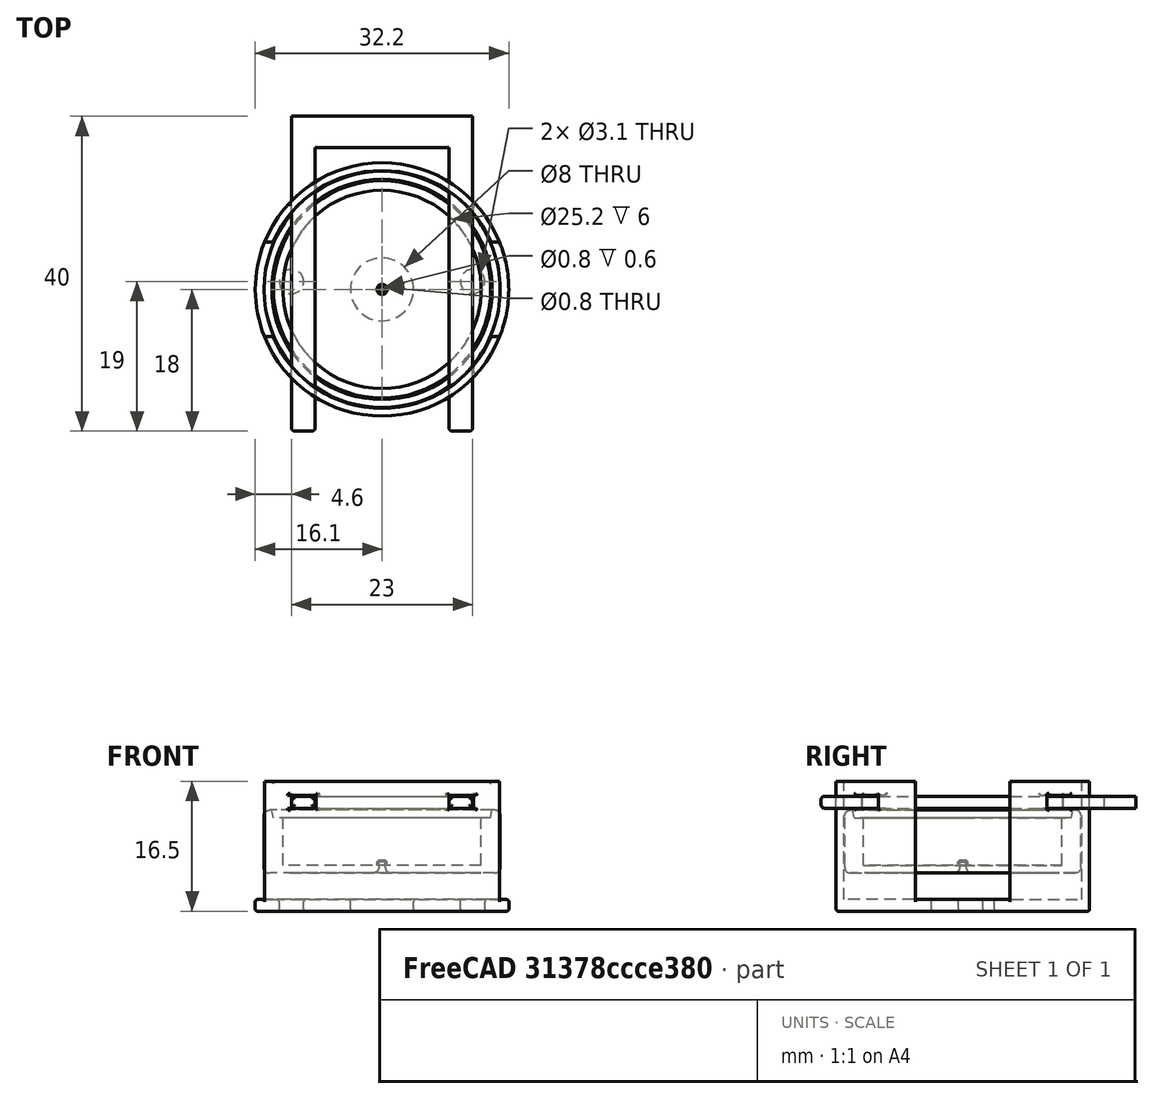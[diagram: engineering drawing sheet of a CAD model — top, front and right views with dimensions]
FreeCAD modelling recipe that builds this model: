
FCSTD DOCUMENT  (FreeCAD 0.18R16131 (Git))
Label: microfluidic_testsetup_v1
License: All rights reserved
LicenseURL: http://en.wikipedia.org/wiki/All_rights_reserved
objects: Part::Cylinder×13, Part::Cut×10, Part::Fillet×7, Part::Box×7, Part::MultiFuse×5, Part::Chamfer×1, Part::Cone×1
note: 44 computed .brp shape members not serialized (recipe doc carries the construction recipe); baked Part::Feature solids carry a one-line shape summary decoded from their .brp

FEATURE [Part::Cylinder] Cylinder
  Angle = 360
  AttacherType = Attacher::AttachEngine3D
  Height = 8
  Radius = 15
FEATURE [Part::Cylinder] Cylinder001
  Angle = 360
  AttacherType = Attacher::AttachEngine3D
  Height = 8
  Radius = 12.6
FEATURE [Part::Cut] Cut
  Base = -> Cylinder
  Tool = -> Cylinder001
FEATURE [Part::Cylinder] Cylinder002
  Angle = 360
  AttacherType = Attacher::AttachEngine3D
  Height = 1
  Radius = 15
FEATURE [Part::MultiFuse] Fusion
  Shapes = -> [Cylinder002,Cut]
FEATURE [Part::Cylinder] Cylinder005
  Angle = 360
  AttacherType = Attacher::AttachEngine3D
  Height = 1
  Radius = 0.4
FEATURE [Part::Cut] Cut001
  Base = -> Fusion
  Tool = -> Cylinder005
FEATURE [Part::Cylinder] Cylinder004
  Angle = 360
  AttacherType = Attacher::AttachEngine3D
  Height = 0.6
  Placement = pos=(0,0,1) rot=(0,0,1;0rad)
  Radius = 0.4
FEATURE [Part::Cylinder] Cylinder003
  Angle = 360
  AttacherType = Attacher::AttachEngine3D
  Height = 0.6
  Placement = pos=(0,0,1) rot=(0,0,1;0rad)
  Radius = 0.65
FEATURE [Part::Cut] Cut002
  Base = -> Cylinder003
  Tool = -> Cylinder004
FEATURE [Part::Chamfer] Chamfer
  Base = -> Cut002
  Edges = 1 edges r=0.2: [Edge1]
FEATURE [Part::Cylinder] Cylinder006
  Angle = 360
  AttacherType = Attacher::AttachEngine3D
  Height = 1
  Placement = pos=(0,0,7) rot=(0,0,1;0rad)
  Radius = 14
FEATURE [Part::Cut] Cut003
  Base = -> Cut001
  Tool = -> Cylinder006
FEATURE [Part::Fillet] Fillet
  Base = -> Cut003
  Edges = 1 edges r=0.7: [Edge5]
FEATURE [Part::Fillet] Fillet001
  Base = -> Fillet
  Edges = 1 edges r=0.7: [Edge7]
FEATURE [Part::Fillet] Fillet002
  Base = -> Fillet001
  Edges = 1 edges r=0.8: [Edge11]
FEATURE [Part::Cone] Cone
  Angle = 360
  AttacherType = Attacher::AttachEngine3D
  Height = 1
  Placement = pos=(0,0,7) rot=(0,0,1;0rad)
  Radius1 = 13.8
  Radius2 = 14
FEATURE [Part::Cylinder] Cylinder007
  Angle = 360
  AttacherType = Attacher::AttachEngine3D
  Height = 1
  Placement = pos=(0,0,7) rot=(0,0,1;0rad)
  Radius = 14
FEATURE [Part::Cut] Cut004
  Base = -> Cylinder007
  Tool = -> Cone
FEATURE [Part::MultiFuse] Fusion001
  Placement = pos=(0,0,3.35) rot=(0,0,1;0rad)
  Shapes = -> [Cut004,Fillet002,Chamfer]
FEATURE [Part::Cylinder] Cylinder008
  Angle = 360
  AttacherType = Attacher::AttachEngine3D
  Height = 16.5
  Placement = pos=(0,0,-1.5) rot=(0,0,1;0rad)
  Radius = 16.1
FEATURE [Part::Cylinder] Cylinder009
  Angle = 360
  AttacherType = Attacher::AttachEngine3D
  Height = 16.5
  Radius = 15.1
FEATURE [Part::Cut] Cut005
  Base = -> Cylinder008
  Tool = -> Cylinder009
FEATURE [Part::Cylinder] Cylinder010
  Angle = 360
  AttacherType = Attacher::AttachEngine3D
  Height = 10
  Placement = pos=(0,0,-2) rot=(0,0,1;0rad)
  Radius = 4
FEATURE [Part::Cut] Cut006
  Base = -> Cut005
  Tool = -> Cylinder010
FEATURE [Part::Box] Box  label="Cube"
  AttacherType = Attacher::AttachEngine3D
  Height = 1.5
  Length = 3
  Placement = pos=(-11.5,-18,11.6) rot=(0,0,1;0rad)
  Width = 36
FEATURE [Part::Box] Box001  label="Cube001"
  AttacherType = Attacher::AttachEngine3D
  Height = 1.5
  Length = 3
  Placement = pos=(8.5,-18,11.6) rot=(0,0,1;0rad)
  Width = 36
FEATURE [Part::Box] Box002  label="Cube002"
  AttacherType = Attacher::AttachEngine3D
  Height = 1.5
  Length = 23
  Placement = pos=(-11.5,18,11.6) rot=(0,0,1;0rad)
  Width = 4
FEATURE [Part::MultiFuse] Fusion002
  Shapes = -> [Box,Box002,Box001]
FEATURE [Part::Box] Box003  label="Cube003"
  AttacherType = Attacher::AttachEngine3D
  Height = 20
  Length = 35
  Placement = pos=(-17.5,-6,0) rot=(0,0,1;0rad)
  Width = 12
FEATURE [Part::Cut] Cut007
  Base = -> Cut006
  Tool = -> Box003
FEATURE [Part::Cylinder] Cylinder011
  Angle = 360
  AttacherType = Attacher::AttachEngine3D
  Height = 10
  Placement = pos=(-11.5,1,-2) rot=(0,0,1;0rad)
  Radius = 1.55
FEATURE [Part::Cylinder] Cylinder012
  Angle = 360
  AttacherType = Attacher::AttachEngine3D
  Height = 10
  Placement = pos=(11.5,1,-2) rot=(0,0,1;0rad)
  Radius = 1.55
FEATURE [Part::MultiFuse] Fusion003
  Shapes = -> [Cylinder012,Cylinder011]
FEATURE [Part::Cut] Cut008
  Base = -> Cut007
  Tool = -> Fusion003
FEATURE [Part::Box] Box004  label="Cube004"
  AttacherType = Attacher::AttachEngine3D
  Height = 1.6
  Length = 3.1
  Placement = pos=(-11.5,-18,11.6) rot=(0,0,1;0rad)
  Width = 36
FEATURE [Part::Box] Box005  label="Cube005"
  AttacherType = Attacher::AttachEngine3D
  Height = 1.5
  Length = 23
  Placement = pos=(-11.5,18,11.6) rot=(0,0,1;0rad)
  Width = 4
FEATURE [Part::Box] Box006  label="Cube006"
  AttacherType = Attacher::AttachEngine3D
  Height = 1.6
  Length = 3.1
  Placement = pos=(8.5,-18,11.6) rot=(0,0,1;0rad)
  Width = 36
FEATURE [Part::MultiFuse] Fusion004
  Shapes = -> [Box004,Box005,Box006]
FEATURE [Part::Cut] Cut009
  Base = -> Cut008
  Tool = -> Fusion004
FEATURE [Part::Fillet] Fillet003
  Base = -> Cut009
  Edges = 12 edges r=0.3: [Edge3,Edge7,Edge10,Edge29,Edge31,Edge35,Edge37,Edge40,Edge47,Edge83,Edge84,Edge85]
FEATURE [Part::Fillet] Fillet004
  Base = -> Fillet003
  Edges = 4 edges r=0.3: [Edge3,Edge35,Edge36,Edge37]
FEATURE [Part::Fillet] Fillet005
  Base = -> Fillet004
  Edges = 32 edges r=0.3: [Edge16,Edge17,Edge18,Edge19,Edge20,Edge21,Edge22,Edge23,Edge24,Edge25,Edge26,Edge27,Edge28,Edge29,Edge30,Edge31,Edge61,Edge64,Edge66,Edge67,Edge69,Edge72,Edge74,Edge75,Edge78,Edge80,Edge82,Edge83,Edge86,Edge88,Edge90,Edge91]
FEATURE [Part::Fillet] Fillet006
  Base = -> Fusion002
  Edges = 8 edges r=0.4: [Edge1,Edge5,Edge6,Edge7,Edge29,Edge32,Edge33,Edge34]
